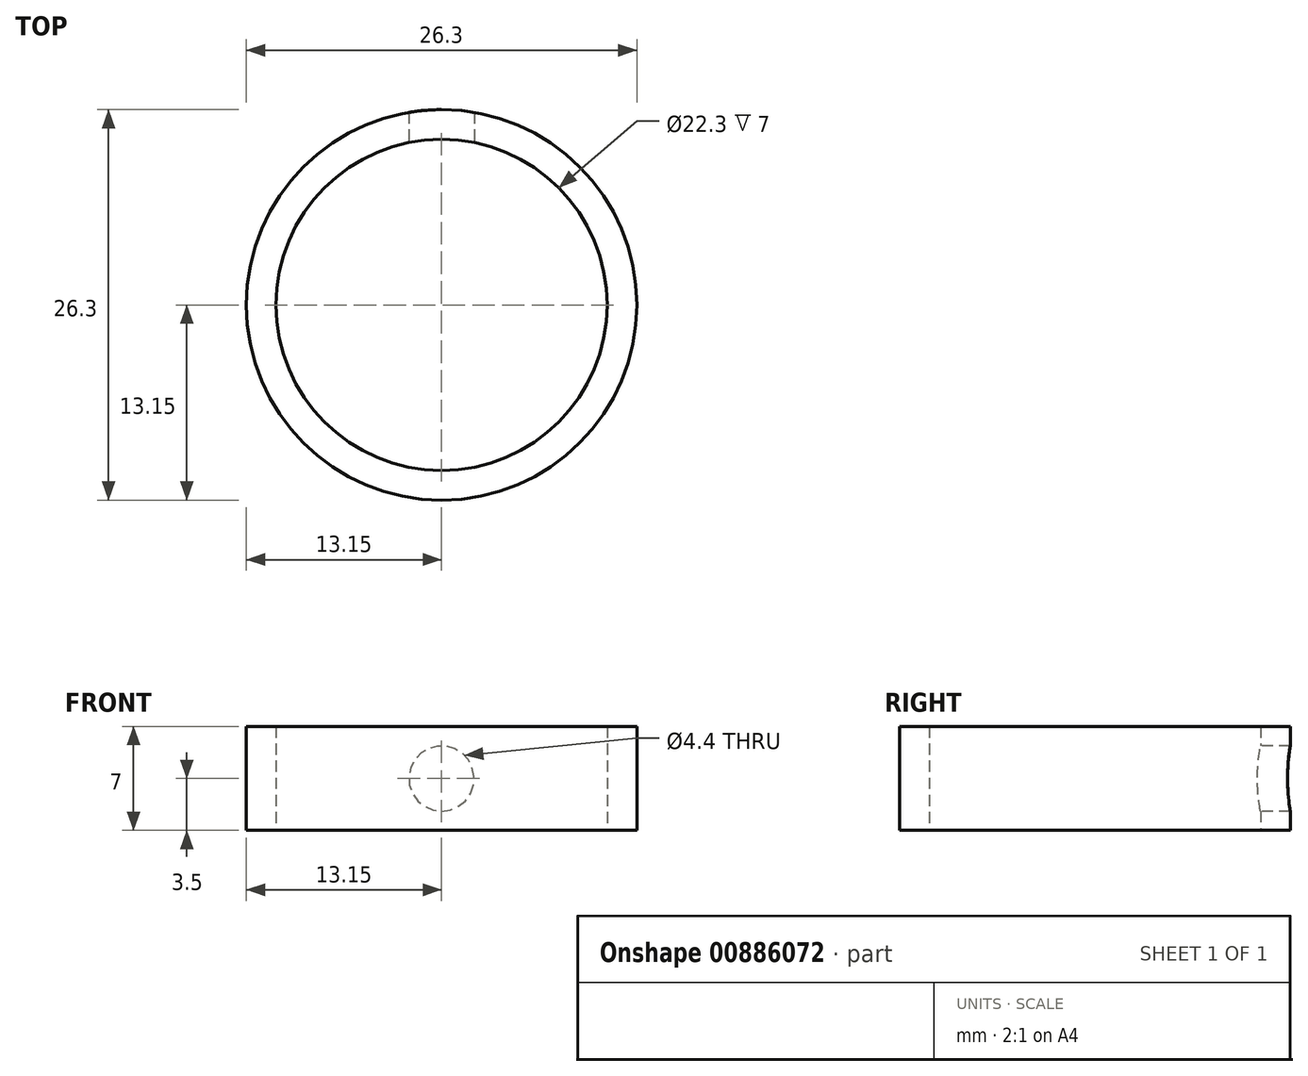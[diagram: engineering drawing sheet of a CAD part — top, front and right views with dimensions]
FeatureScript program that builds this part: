
annotation { "Feature Type Name" : "Feature", "Feature Type Description" : "" }
export const myFeature = defineFeature(function(context is Context, id is Id, definition is map)
    precondition{}
    {
        {
            var Q0;
            Q0=qCreatedBy(makeId("Top.planeOp"),FACE);
            var sketch = newSketch(context, id + "F0", { "sketchPlane" : qUnion([Q0])});
            skCircle(sketch, "E0", {"center": v(0, 0) * mm, "radius": 11.15 * mm});
            skCircle(sketch, "E1", {"center": v(0, 0) * mm, "radius": 13.15 * mm});
            skSolve(sketch);
        }
        {
            var Q0;
            Q0=makeQuery(id+"F0.imprint","IMPRINT",FACE,{"disambiguationData":[TD([[makeQuery(id+"F0.imprint","IMPRINT",EDGE,{"derivedFrom":sQuery(id+"F0.wireOp",EDGE,"E0")}),-1.0]])]});
            extrude(context, id + "F1", {"entities" : qUnion([Q0]), "endBound" : BoundingType.SYMMETRIC, "depth" : 7 * mm, "offsetDistance" : 25 * mm});
        }
        {
            var Q0;
            Q0=qCreatedBy(makeId("Front.planeOp"),FACE);
            var sketch = newSketch(context, id + "F2", { "sketchPlane" : qUnion([Q0])});
            skCircle(sketch, "E2", {"center": v(0, 0) * mm, "radius": 2.2 * mm});
            skLineSegment(sketch, "E3", {"start": v(0, 0) * mm, "end": v(0, 10.34) * mm, "construction": true});
            skSolve(sketch);
        }
        {
            var Q0;
            Q0 = qSketchRegion(id + "F2", true);
            extrude(context, id + "F3", {"entities" : qUnion([Q0]), "operationType" : NewBodyOperationType.REMOVE, "oppositeDirection" : true, "depth" : 25 * mm, "offsetDistance" : 25 * mm});
        }
    });
